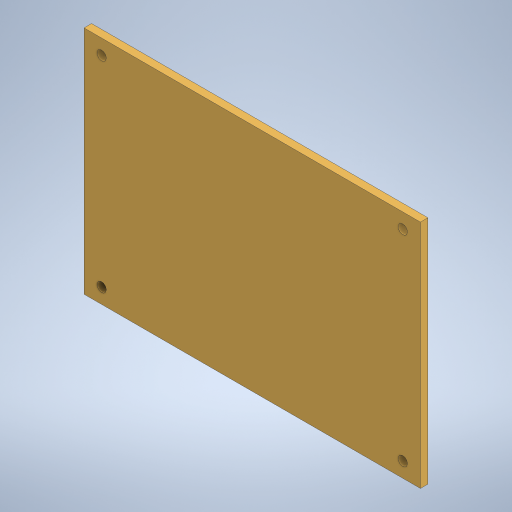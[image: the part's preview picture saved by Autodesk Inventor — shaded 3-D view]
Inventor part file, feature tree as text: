
AUTODESK INVENTOR PART (.ipt)
format: ipt  version: 2023.1 (Build 271208000, 208)  size: 211,456 bytes
history: native  units: mm
features: other x1, extrude x1, sketch x1
ambient origin geometry x8: Origin, YZ Plane, XZ Plane, XY Plane, X Axis, Y Axis, Z Axis, Center Point
bodies: Body1 (feature_tree)
feature tree (3):
  other  "솔리드1"
  extrude  "돌출1"  Depth=71.6mm
  sketch  "스케치1"
